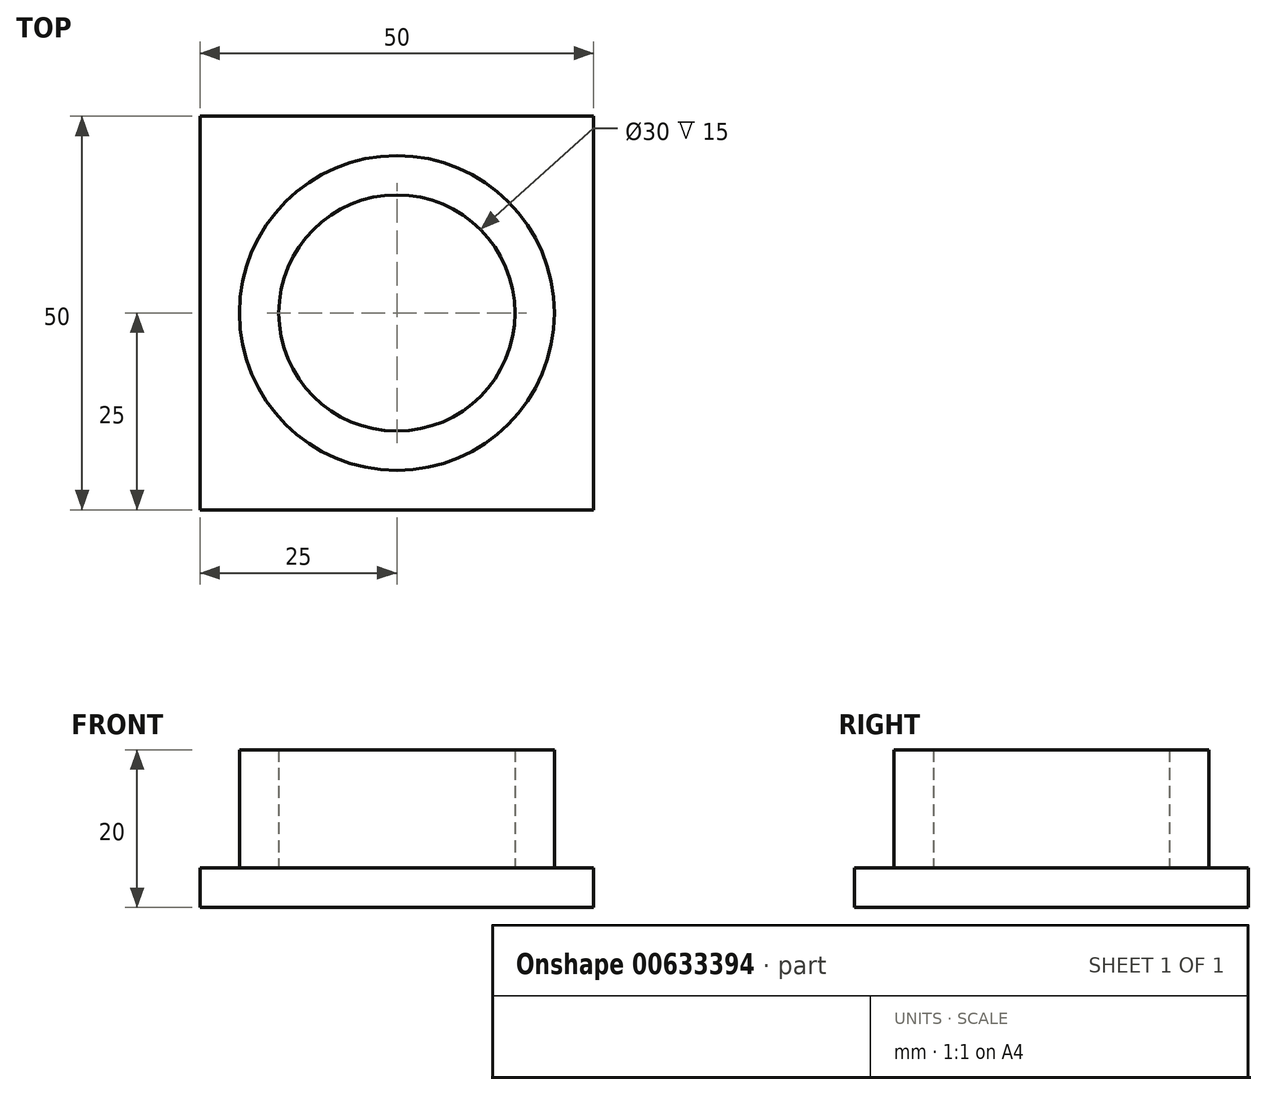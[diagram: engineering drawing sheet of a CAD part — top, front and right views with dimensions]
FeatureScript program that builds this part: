
annotation { "Feature Type Name" : "Feature", "Feature Type Description" : "" }
export const myFeature = defineFeature(function(context is Context, id is Id, definition is map)
    precondition{}
    {
        {
            var Q0;
            Q0=qCreatedBy(makeId("Top.planeOp"),FACE);
            var sketch = newSketch(context, id + "F0", { "sketchPlane" : qUnion([Q0])});
            skLineSegment(sketch, "E0.bottom", {"start": v(0, 0) * mm, "end": v(-50, 0) * mm});
            skLineSegment(sketch, "E0.top", {"start": v(0, 50) * mm, "end": v(-50, 50) * mm});
            skLineSegment(sketch, "E0.left", {"start": v(0, 0) * mm, "end": v(0, 50) * mm});
            skLineSegment(sketch, "E0.right", {"start": v(-50, 0) * mm, "end": v(-50, 50) * mm});
            skSolve(sketch);
        }
        {
            var Q0;
            Q0 = qSketchRegion(id + "F0", true);
            extrude(context, id + "F1", {"entities" : qUnion([Q0]), "depth" : 5 * mm, "offsetDistance" : 25 * mm});
        }
        {
            var Q0;
            Q0=makeQuery(id+"F1.opExtrude","CAP_FACE",FACE,{"disambiguationData":[OSD([sQuery(id+"F0.wireOp",EDGE,"E0.bottom"),sQuery(id+"F0.wireOp",EDGE,"E0.top"),sQuery(id+"F0.wireOp",EDGE,"E0.left"),sQuery(id+"F0.wireOp",EDGE,"E0.right")])],"isStart":false});
            var sketch = newSketch(context, id + "F2", { "sketchPlane" : qUnion([Q0])});
            skCircle(sketch, "E1", {"center": v(-25, 25) * mm, "radius": 20 * mm});
            skCircle(sketch, "E2", {"center": v(-25, 25) * mm, "radius": 15 * mm});
            skSolve(sketch);
        }
        {
            var Q0;
            Q0 = qSketchRegion(id + "F2", true);
            extrude(context, id + "F3", {"entities" : qUnion([Q0]), "operationType" : NewBodyOperationType.ADD, "depth" : 15 * mm, "offsetDistance" : 25 * mm});
        }
    });
